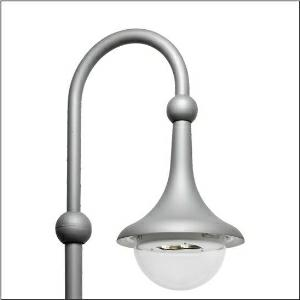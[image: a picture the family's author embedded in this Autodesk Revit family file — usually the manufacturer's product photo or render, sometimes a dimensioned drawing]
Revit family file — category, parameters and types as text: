
# Revit family: grosse_glocke___st1_2a_5xa1563k1b108_1a11
name_source: partatom
category: Lighting Fixtures
units: mm (PartAtom-declared; Revit-internal decimal feet)

## family parameters
Cut with Voids When Loaded = No
Host = Face
Light Source = No
Part Type = Normal
Room Calculation Point = No
Round Connector Dimension = Use Diameter
Shared = No

## types (1)
- --- (1 x LED, 3320 lm, 23.4 W, 4000K)
    Apparent Load = 23 VA
    CIE Flux Codes = 29 66 95 99 100
    Color Rendering = 70
    Color Temperature = 4000K
    Default Elevation = 1800 mm
    Description = Large Bell, mast luminaire, primary light control with 3 zone facetted reflector, of plastic, silver coated, primary optical cover: enclosure, of PMMA, transparent, light distribution: ST1.2a, light emission: direct distribution, primary light characteristic: asymmetric, installation type: suspended mounting, LED, High Power LED, rated luminous flux: 3.320lm, luminous efficacy: 142lm/W, light colour: 740, colour temperature: 4000K, control gear: Plus, control: flexible luminous flux parameterisation, time-dependent luminous flux control, constant luminous flux control, digital communication interface, power reduction, electronic power reduction, mains connection: 230..240V, AC, 50/60Hz, start of lifetime: 23W, end of service life: 24W, reduction: 12W, luminaire housing, bell-shaped, of glass-fibre reinforced polyester, coated, Siteco® metallic grey (DB 702S), please order curved mast extension separately, diameter: 530mm, height: 695mm, mounting height: 4..6m, protection rating (complete): IP54, insulation class (complete): insulation class II (safety insulation), certification: CE, ENEC, VDE, impact resistance: IK08, standard-compliant lighting for roads and squares, packaging unit: 1 piece

Light Distribution: ST1.2a
    Height = 695 mm
    Lamp = 1 x LED
    Lamp Light Flux = 3320 lm
    Lamp Power = 23.4 W
    Lamp count = 1
    Length = 530 mm
    Luminous efficacy = 142 lm/W
    Manufacturer = Siteco
    ModVariant = No
    Model = 5XA1563K1B108
    Number of Poles = 1
    OnlyDefault = Yes
    Power Factor = 1
    Product Name = Große Glocke | ST1.2a
    Product group = mast luminaire | pylon annexe
    ProductGroupID = 6200
    Protection Class = Protection class II
    Protection Degree = IP 54
    RLX_Detail_Level = 1
    RLX_Emergency_Light_Flux = 0 lm
    RLX_Emergency_Type = 0
    RLX_Emergency_Type_DB = No
    RlxData = <blob elided: 52973 chars, md5=b9b61835>
    Socket = socket
    Standby Power = 0 W
    System Light Flux = 3320 lm
    System Power = 23 W
    Type Comments = factory setting: luminous flux: 100 % | dim-lin: 254 | 460 mA
    Type Image = l_1347688.jpg
    URL = http://relux.com
    VarID = @adj_218865
    Voltage = 0 V
    Weight = 0.00 kg
    Width = 0 mm  [stored 0 ft]

note: [stored X ft] marks values corroborated as IEEE doubles in the binary element streams (Revit-internal decimal feet)

## geometry (parser evidence)
native form markers: Blend x4, Sweep x12
no freeform markers — native parametric forms only
